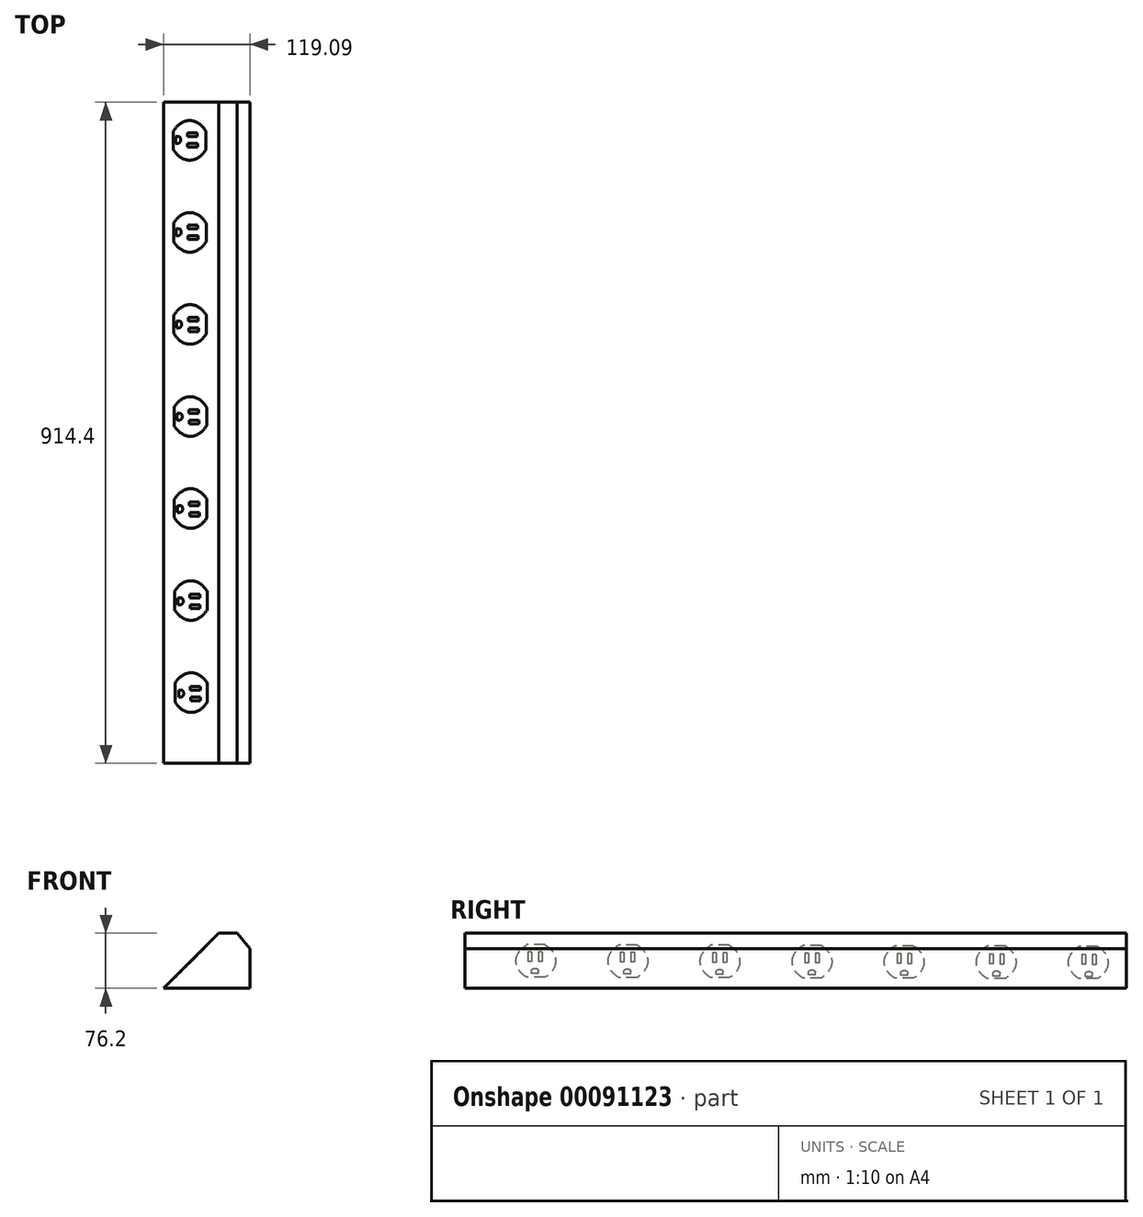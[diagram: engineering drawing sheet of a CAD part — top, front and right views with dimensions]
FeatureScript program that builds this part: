
annotation { "Feature Type Name" : "Feature", "Feature Type Description" : "" }
export const myFeature = defineFeature(function(context is Context, id is Id, definition is map)
    precondition{}
    {
        {
            var Q0;
            Q0=qCreatedBy(makeId("Front.planeOp"),FACE);
            var sketch = newSketch(context, id + "F0", { "sketchPlane" : qUnion([Q0])});
            skLineSegment(sketch, "E0", {"start": v(0, 0) * mm, "end": v(-76.2, 0) * mm});
            skLineSegment(sketch, "E1", {"start": v(-76.2, 0) * mm, "end": v(0, 76.2) * mm});
            skLineSegment(sketch, "E2", {"start": v(0, 76.2) * mm, "end": v(25.08, 76.2) * mm});
            skLineSegment(sketch, "E3", {"start": v(25.08, 76.2) * mm, "end": v(42.89, 54.98) * mm});
            skLineSegment(sketch, "E4", {"start": v(42.89, 54.98) * mm, "end": v(42.89, 0) * mm});
            skLineSegment(sketch, "E5", {"start": v(42.89, 0) * mm, "end": v(0, 0) * mm});
            skSolve(sketch);
        }
        {
            var Q0;
            Q0 = qSketchRegion(id + "F0", true);
            extrude(context, id + "F1", {"entities" : qUnion([Q0]), "endBound" : BoundingType.SYMMETRIC, "depth" : 914.4 * mm});
        }
        {
            var Q0;
            Q0=makeQuery(id+"F1.opExtrude","SWEPT_FACE",FACE,{"disambiguationData":[OSD([sQuery(id+"F0.wireOp",EDGE,"E1")])]});
            var sketch = newSketch(context, id + "F2", { "sketchPlane" : qUnion([Q0])});
            skLineSegment(sketch, "E6", {"start": v(-417.1, 28.48) * mm, "end": v(-391.7, 28.48) * mm});
            skLineSegment(sketch, "E7", {"start": v(-417.1, -35.02) * mm, "end": v(-391.7, -35.02) * mm});
            skArc(sketch, "E8", {"start": v(-417.1, 28.48) * mm, "mid": v(-431.8, -3.27) * mm, "end": v(-417.1, -35.02) * mm});
            skArc(sketch, "E9", {"start": v(-391.7, -35.02) * mm, "mid": v(-377, -3.27) * mm, "end": v(-391.7, 28.48) * mm});
            skLineSegment(sketch, "E10.1.0.0", {"start": v(-289.82, 28.97) * mm, "end": v(-264.42, 28.97) * mm});
            skArc(sketch, "E10.1.0.1", {"start": v(-289.82, 28.97) * mm, "mid": v(-304.52, -2.78) * mm, "end": v(-289.82, -34.53) * mm});
            skLineSegment(sketch, "E10.1.0.2", {"start": v(-289.82, -34.53) * mm, "end": v(-264.42, -34.53) * mm});
            skArc(sketch, "E10.1.0.3", {"start": v(-264.42, -34.53) * mm, "mid": v(-249.72, -2.78) * mm, "end": v(-264.42, 28.97) * mm});
            skLineSegment(sketch, "E10.2.0.0", {"start": v(-162.54, 29.45) * mm, "end": v(-137.14, 29.45) * mm});
            skArc(sketch, "E10.2.0.1", {"start": v(-162.54, 29.45) * mm, "mid": v(-177.24, -2.3) * mm, "end": v(-162.54, -34.05) * mm});
            skLineSegment(sketch, "E10.2.0.2", {"start": v(-162.54, -34.05) * mm, "end": v(-137.14, -34.05) * mm});
            skArc(sketch, "E10.2.0.3", {"start": v(-137.14, -34.05) * mm, "mid": v(-122.43, -2.3) * mm, "end": v(-137.14, 29.45) * mm});
            skLineSegment(sketch, "E10.3.0.0", {"start": v(-35.25, 29.94) * mm, "end": v(-9.85, 29.94) * mm});
            skArc(sketch, "E10.3.0.1", {"start": v(-35.25, 29.94) * mm, "mid": v(-49.95, -1.81) * mm, "end": v(-35.25, -33.56) * mm});
            skLineSegment(sketch, "E10.3.0.2", {"start": v(-35.25, -33.56) * mm, "end": v(-9.85, -33.56) * mm});
            skArc(sketch, "E10.3.0.3", {"start": v(-9.85, -33.56) * mm, "mid": v(4.85, -1.81) * mm, "end": v(-9.85, 29.94) * mm});
            skLineSegment(sketch, "E10.4.0.0", {"start": v(92.03, 30.42) * mm, "end": v(117.43, 30.42) * mm});
            skArc(sketch, "E10.4.0.1", {"start": v(92.03, 30.42) * mm, "mid": v(77.33, -1.33) * mm, "end": v(92.03, -33.08) * mm});
            skLineSegment(sketch, "E10.4.0.2", {"start": v(92.03, -33.08) * mm, "end": v(117.43, -33.08) * mm});
            skArc(sketch, "E10.4.0.3", {"start": v(117.43, -33.08) * mm, "mid": v(132.13, -1.33) * mm, "end": v(117.43, 30.42) * mm});
            skLineSegment(sketch, "E10.5.0.0", {"start": v(219.31, 30.9) * mm, "end": v(244.71, 30.9) * mm});
            skArc(sketch, "E10.5.0.1", {"start": v(219.31, 30.9) * mm, "mid": v(204.6, -0.85) * mm, "end": v(219.31, -32.6) * mm});
            skLineSegment(sketch, "E10.5.0.2", {"start": v(219.31, -32.6) * mm, "end": v(244.71, -32.6) * mm});
            skArc(sketch, "E10.5.0.3", {"start": v(244.71, -32.6) * mm, "mid": v(259.41, -0.85) * mm, "end": v(244.71, 30.9) * mm});
            skLineSegment(sketch, "E10.6.0.0", {"start": v(346.6, 31.39) * mm, "end": v(372, 31.39) * mm});
            skArc(sketch, "E10.6.0.1", {"start": v(346.6, 31.39) * mm, "mid": v(331.9, -0.36) * mm, "end": v(346.6, -32.11) * mm});
            skLineSegment(sketch, "E10.6.0.2", {"start": v(346.6, -32.11) * mm, "end": v(372, -32.11) * mm});
            skArc(sketch, "E10.6.0.3", {"start": v(372, -32.11) * mm, "mid": v(386.7, -0.36) * mm, "end": v(372, 31.39) * mm});
            skLineSegment(sketch, "E10.direction1", {"start": v(-417.1, 28.48) * mm, "end": v(-289.82, 28.97) * mm, "construction": true});
            skLineSegment(sketch, "E11.bottom", {"start": v(-415.08, 11.56) * mm, "end": v(-410, 11.56) * mm});
            skLineSegment(sketch, "E11.top", {"start": v(-415.08, -7.49) * mm, "end": v(-410, -7.49) * mm});
            skLineSegment(sketch, "E11.left", {"start": v(-415.08, 11.56) * mm, "end": v(-415.08, -7.49) * mm});
            skLineSegment(sketch, "E11.right", {"start": v(-410, 11.56) * mm, "end": v(-410, -7.49) * mm});
            skLineSegment(sketch, "E12.bottom", {"start": v(-400.52, 11.94) * mm, "end": v(-395.44, 11.94) * mm});
            skLineSegment(sketch, "E12.top", {"start": v(-400.52, -7.11) * mm, "end": v(-395.44, -7.11) * mm});
            skLineSegment(sketch, "E12.left", {"start": v(-400.52, 11.94) * mm, "end": v(-400.52, -7.11) * mm});
            skLineSegment(sketch, "E12.right", {"start": v(-395.44, 11.94) * mm, "end": v(-395.44, -7.11) * mm});
            skLineSegment(sketch, "E13.bottom", {"start": v(-410, -30.75) * mm, "end": v(-400.52, -30.75) * mm});
            skLineSegment(sketch, "E13.left", {"start": v(-410, -30.75) * mm, "end": v(-410, -25.43) * mm});
            skLineSegment(sketch, "E13.right", {"start": v(-400.52, -30.75) * mm, "end": v(-400.52, -25.5) * mm});
            skArc(sketch, "E14", {"start": v(-410, -25.43) * mm, "mid": v(-405.23, -20.7) * mm, "end": v(-400.52, -25.5) * mm});
            skLineSegment(sketch, "E15.1.0.0", {"start": v(-267.8, 12.91) * mm, "end": v(-267.8, -6.14) * mm});
            skLineSegment(sketch, "E15.1.0.1", {"start": v(-272.89, 12.91) * mm, "end": v(-267.8, 12.91) * mm});
            skLineSegment(sketch, "E15.1.0.2", {"start": v(-272.89, 12.91) * mm, "end": v(-272.89, -6.14) * mm});
            skLineSegment(sketch, "E15.1.0.3", {"start": v(-282.37, 12.54) * mm, "end": v(-282.37, -6.51) * mm});
            skLineSegment(sketch, "E15.1.0.4", {"start": v(-287.45, -6.51) * mm, "end": v(-282.37, -6.51) * mm});
            skLineSegment(sketch, "E15.1.0.5", {"start": v(-287.45, 12.54) * mm, "end": v(-287.45, -6.51) * mm});
            skLineSegment(sketch, "E15.1.0.6", {"start": v(-287.45, 12.54) * mm, "end": v(-282.37, 12.54) * mm});
            skLineSegment(sketch, "E15.1.0.7", {"start": v(-282.37, -29.78) * mm, "end": v(-272.89, -29.78) * mm});
            skLineSegment(sketch, "E15.1.0.8", {"start": v(-282.37, -29.78) * mm, "end": v(-282.37, -24.46) * mm});
            skLineSegment(sketch, "E15.1.0.9", {"start": v(-272.89, -29.78) * mm, "end": v(-272.89, -24.53) * mm});
            skArc(sketch, "E15.1.0.10", {"start": v(-282.37, -24.46) * mm, "mid": v(-277.6, -19.72) * mm, "end": v(-272.89, -24.53) * mm});
            skLineSegment(sketch, "E15.1.0.11", {"start": v(-272.89, -6.14) * mm, "end": v(-267.8, -6.14) * mm});
            skLineSegment(sketch, "E15.2.0.0", {"start": v(-140.18, 13.89) * mm, "end": v(-140.18, -5.16) * mm});
            skLineSegment(sketch, "E15.2.0.1", {"start": v(-145.26, 13.89) * mm, "end": v(-140.18, 13.89) * mm});
            skLineSegment(sketch, "E15.2.0.2", {"start": v(-145.26, 13.89) * mm, "end": v(-145.26, -5.16) * mm});
            skLineSegment(sketch, "E15.2.0.3", {"start": v(-154.73, 13.51) * mm, "end": v(-154.73, -5.54) * mm});
            skLineSegment(sketch, "E15.2.0.4", {"start": v(-159.81, -5.54) * mm, "end": v(-154.73, -5.54) * mm});
            skLineSegment(sketch, "E15.2.0.5", {"start": v(-159.81, 13.51) * mm, "end": v(-159.81, -5.54) * mm});
            skLineSegment(sketch, "E15.2.0.6", {"start": v(-159.81, 13.51) * mm, "end": v(-154.73, 13.51) * mm});
            skLineSegment(sketch, "E15.2.0.7", {"start": v(-154.73, -28.8) * mm, "end": v(-145.26, -28.8) * mm});
            skLineSegment(sketch, "E15.2.0.8", {"start": v(-154.73, -28.8) * mm, "end": v(-154.73, -23.49) * mm});
            skLineSegment(sketch, "E15.2.0.9", {"start": v(-145.26, -28.8) * mm, "end": v(-145.26, -23.55) * mm});
            skArc(sketch, "E15.2.0.10", {"start": v(-154.73, -23.49) * mm, "mid": v(-149.96, -18.75) * mm, "end": v(-145.26, -23.55) * mm});
            skLineSegment(sketch, "E15.2.0.11", {"start": v(-145.26, -5.16) * mm, "end": v(-140.18, -5.16) * mm});
            skLineSegment(sketch, "E15.3.0.0", {"start": v(-12.55, 14.86) * mm, "end": v(-12.55, -4.19) * mm});
            skLineSegment(sketch, "E15.3.0.1", {"start": v(-17.63, 14.86) * mm, "end": v(-12.55, 14.86) * mm});
            skLineSegment(sketch, "E15.3.0.2", {"start": v(-17.63, 14.86) * mm, "end": v(-17.63, -4.19) * mm});
            skLineSegment(sketch, "E15.3.0.3", {"start": v(-27.1, 14.49) * mm, "end": v(-27.1, -4.56) * mm});
            skLineSegment(sketch, "E15.3.0.4", {"start": v(-32.18, -4.56) * mm, "end": v(-27.1, -4.56) * mm});
            skLineSegment(sketch, "E15.3.0.5", {"start": v(-32.18, 14.49) * mm, "end": v(-32.18, -4.56) * mm});
            skLineSegment(sketch, "E15.3.0.6", {"start": v(-32.18, 14.49) * mm, "end": v(-27.1, 14.49) * mm});
            skLineSegment(sketch, "E15.3.0.7", {"start": v(-27.1, -27.83) * mm, "end": v(-17.63, -27.83) * mm});
            skLineSegment(sketch, "E15.3.0.8", {"start": v(-27.1, -27.83) * mm, "end": v(-27.1, -22.51) * mm});
            skLineSegment(sketch, "E15.3.0.9", {"start": v(-17.63, -27.83) * mm, "end": v(-17.63, -22.58) * mm});
            skArc(sketch, "E15.3.0.10", {"start": v(-27.1, -22.51) * mm, "mid": v(-22.33, -17.77) * mm, "end": v(-17.63, -22.58) * mm});
            skLineSegment(sketch, "E15.3.0.11", {"start": v(-17.63, -4.19) * mm, "end": v(-12.55, -4.19) * mm});
            skLineSegment(sketch, "E15.4.0.0", {"start": v(115.09, 15.84) * mm, "end": v(115.09, -3.21) * mm});
            skLineSegment(sketch, "E15.4.0.1", {"start": v(110, 15.84) * mm, "end": v(115.09, 15.84) * mm});
            skLineSegment(sketch, "E15.4.0.2", {"start": v(110, 15.84) * mm, "end": v(110, -3.21) * mm});
            skLineSegment(sketch, "E15.4.0.3", {"start": v(100.53, 15.46) * mm, "end": v(100.53, -3.59) * mm});
            skLineSegment(sketch, "E15.4.0.4", {"start": v(95.45, -3.59) * mm, "end": v(100.53, -3.59) * mm});
            skLineSegment(sketch, "E15.4.0.5", {"start": v(95.45, 15.46) * mm, "end": v(95.45, -3.59) * mm});
            skLineSegment(sketch, "E15.4.0.6", {"start": v(95.45, 15.46) * mm, "end": v(100.53, 15.46) * mm});
            skLineSegment(sketch, "E15.4.0.7", {"start": v(100.53, -26.86) * mm, "end": v(110, -26.86) * mm});
            skLineSegment(sketch, "E15.4.0.8", {"start": v(100.53, -26.86) * mm, "end": v(100.53, -21.54) * mm});
            skLineSegment(sketch, "E15.4.0.9", {"start": v(110, -26.86) * mm, "end": v(110, -21.6) * mm});
            skArc(sketch, "E15.4.0.10", {"start": v(100.53, -21.54) * mm, "mid": v(105.3, -16.8) * mm, "end": v(110, -21.6) * mm});
            skLineSegment(sketch, "E15.4.0.11", {"start": v(110, -3.21) * mm, "end": v(115.09, -3.21) * mm});
            skLineSegment(sketch, "E15.5.0.0", {"start": v(242.72, 16.81) * mm, "end": v(242.72, -2.24) * mm});
            skLineSegment(sketch, "E15.5.0.1", {"start": v(237.64, 16.81) * mm, "end": v(242.72, 16.81) * mm});
            skLineSegment(sketch, "E15.5.0.2", {"start": v(237.64, 16.81) * mm, "end": v(237.64, -2.24) * mm});
            skLineSegment(sketch, "E15.5.0.3", {"start": v(228.16, 16.44) * mm, "end": v(228.16, -2.61) * mm});
            skLineSegment(sketch, "E15.5.0.4", {"start": v(223.08, -2.61) * mm, "end": v(228.16, -2.61) * mm});
            skLineSegment(sketch, "E15.5.0.5", {"start": v(223.08, 16.44) * mm, "end": v(223.08, -2.61) * mm});
            skLineSegment(sketch, "E15.5.0.6", {"start": v(223.08, 16.44) * mm, "end": v(228.16, 16.44) * mm});
            skLineSegment(sketch, "E15.5.0.7", {"start": v(228.16, -25.88) * mm, "end": v(237.64, -25.88) * mm});
            skLineSegment(sketch, "E15.5.0.8", {"start": v(228.16, -25.88) * mm, "end": v(228.16, -20.56) * mm});
            skLineSegment(sketch, "E15.5.0.9", {"start": v(237.64, -25.88) * mm, "end": v(237.64, -20.63) * mm});
            skArc(sketch, "E15.5.0.10", {"start": v(228.16, -20.56) * mm, "mid": v(232.93, -15.82) * mm, "end": v(237.64, -20.63) * mm});
            skLineSegment(sketch, "E15.5.0.11", {"start": v(237.64, -2.24) * mm, "end": v(242.72, -2.24) * mm});
            skLineSegment(sketch, "E15.6.0.0", {"start": v(370.35, 17.79) * mm, "end": v(370.35, -1.26) * mm});
            skLineSegment(sketch, "E15.6.0.1", {"start": v(365.27, 17.79) * mm, "end": v(370.35, 17.79) * mm});
            skLineSegment(sketch, "E15.6.0.2", {"start": v(365.27, 17.79) * mm, "end": v(365.27, -1.26) * mm});
            skLineSegment(sketch, "E15.6.0.3", {"start": v(355.8, 17.41) * mm, "end": v(355.8, -1.64) * mm});
            skLineSegment(sketch, "E15.6.0.4", {"start": v(350.71, -1.64) * mm, "end": v(355.8, -1.64) * mm});
            skLineSegment(sketch, "E15.6.0.5", {"start": v(350.71, 17.41) * mm, "end": v(350.71, -1.64) * mm});
            skLineSegment(sketch, "E15.6.0.6", {"start": v(350.71, 17.41) * mm, "end": v(355.8, 17.41) * mm});
            skLineSegment(sketch, "E15.6.0.7", {"start": v(355.8, -24.9) * mm, "end": v(365.27, -24.9) * mm});
            skLineSegment(sketch, "E15.6.0.8", {"start": v(355.8, -24.9) * mm, "end": v(355.8, -19.59) * mm});
            skLineSegment(sketch, "E15.6.0.9", {"start": v(365.27, -24.9) * mm, "end": v(365.27, -19.65) * mm});
            skArc(sketch, "E15.6.0.10", {"start": v(355.8, -19.59) * mm, "mid": v(360.56, -14.85) * mm, "end": v(365.27, -19.65) * mm});
            skLineSegment(sketch, "E15.6.0.11", {"start": v(365.27, -1.26) * mm, "end": v(370.35, -1.26) * mm});
            skLineSegment(sketch, "E15.direction1", {"start": v(-395.44, -7.11) * mm, "end": v(-267.8, -6.14) * mm, "construction": true});
            skSolve(sketch);
        }
        {
            var Q0;
            Q0 = qSketchRegion(id + "F2", true);
            extrude(context, id + "F3", {"entities" : qUnion([Q0]), "operationType" : NewBodyOperationType.ADD, "depth" : 1 / 203.2 * mm});
        }
    });
